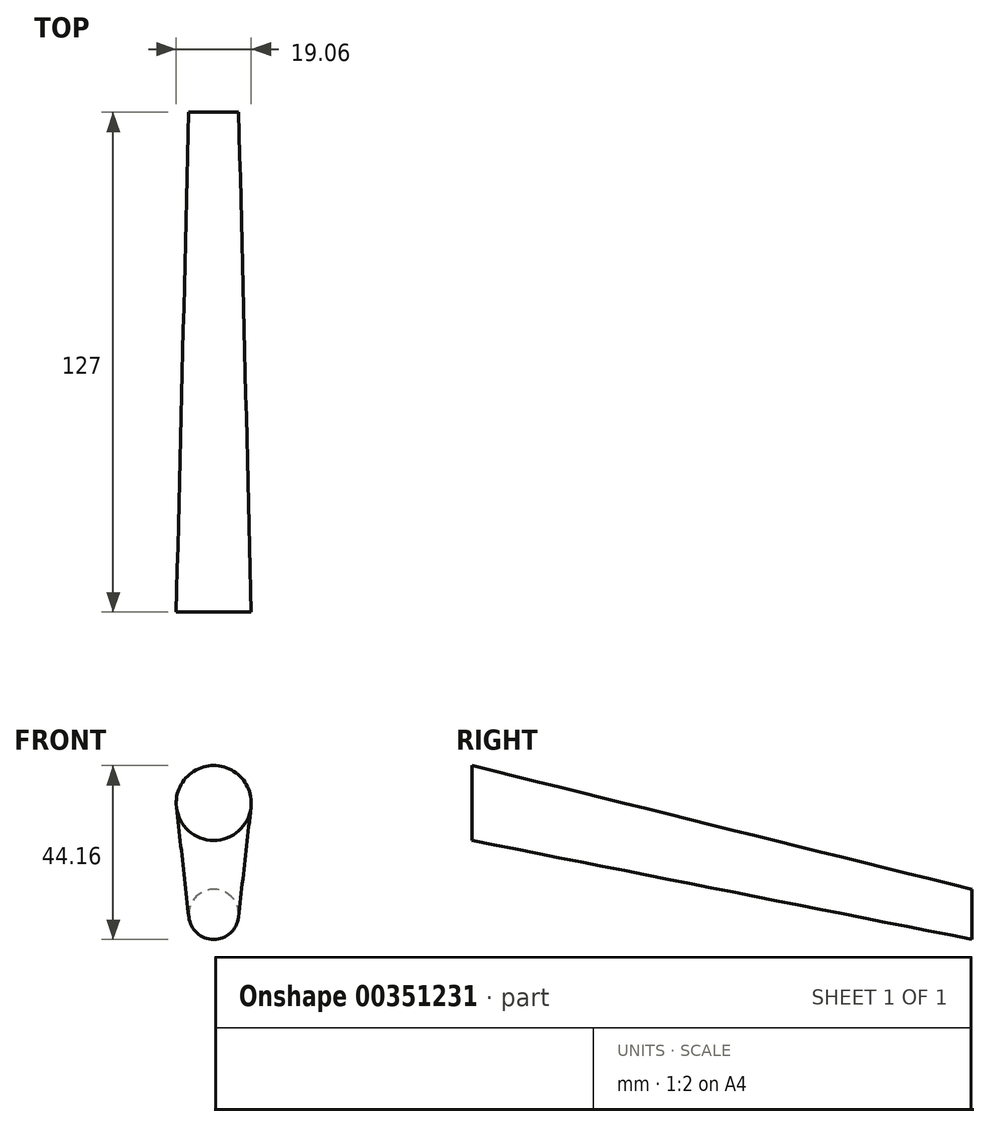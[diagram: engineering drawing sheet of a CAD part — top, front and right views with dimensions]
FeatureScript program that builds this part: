
annotation { "Feature Type Name" : "Feature", "Feature Type Description" : "" }
export const myFeature = defineFeature(function(context is Context, id is Id, definition is map)
    precondition{}
    {
        {
            var Q0;
            Q0=qCreatedBy(makeId("Front.planeOp"),FACE);
            cPlane(context, id + "F0", {"entities" : qUnion([Q0]), "cplaneType" : CPlaneType.OFFSET, "offset" : 127 * mm, "width" : 152.4 * mm, "height" : 152.4 * mm});
        }
        {
            var Q0;
            Q0=qCreatedBy(id+"F0.planeOp",FACE);
            var sketch = newSketch(context, id + "F1", { "sketchPlane" : qUnion([Q0])});
            skCircle(sketch, "E0", {"center": v(0, 28.29) * mm, "radius": 9.53 * mm});
            skSolve(sketch);
        }
        {
            var Q0;
            Q0=qCreatedBy(makeId("Front.planeOp"),FACE);
            var sketch = newSketch(context, id + "F2", { "sketchPlane" : qUnion([Q0])});
            skCircle(sketch, "E1", {"center": v(0, 0) * mm, "radius": 6.35 * mm});
            skSolve(sketch);
        }
        {
            var Q0;
            Q0=makeQuery(id+"F2.imprint","IMPRINT",FACE,{"disambiguationData":[TD([[makeQuery(id+"F2.imprint","IMPRINT",EDGE,{"derivedFrom":sQuery(id+"F2.wireOp",EDGE,"E1")}),1.0]])]});
            var Q1;
            Q1=makeQuery(id+"F1.imprint","IMPRINT",FACE,{"disambiguationData":[TD([[makeQuery(id+"F1.imprint","IMPRINT",EDGE,{"derivedFrom":sQuery(id+"F1.wireOp",EDGE,"E0")}),1.0]])]});
            loft(context, id + "F3", {"sheetProfilesArray" : [{ "sheetProfileEntities" : qUnion([Q0]) }, { "sheetProfileEntities" : qUnion([Q1]) }]});
        }
    });
